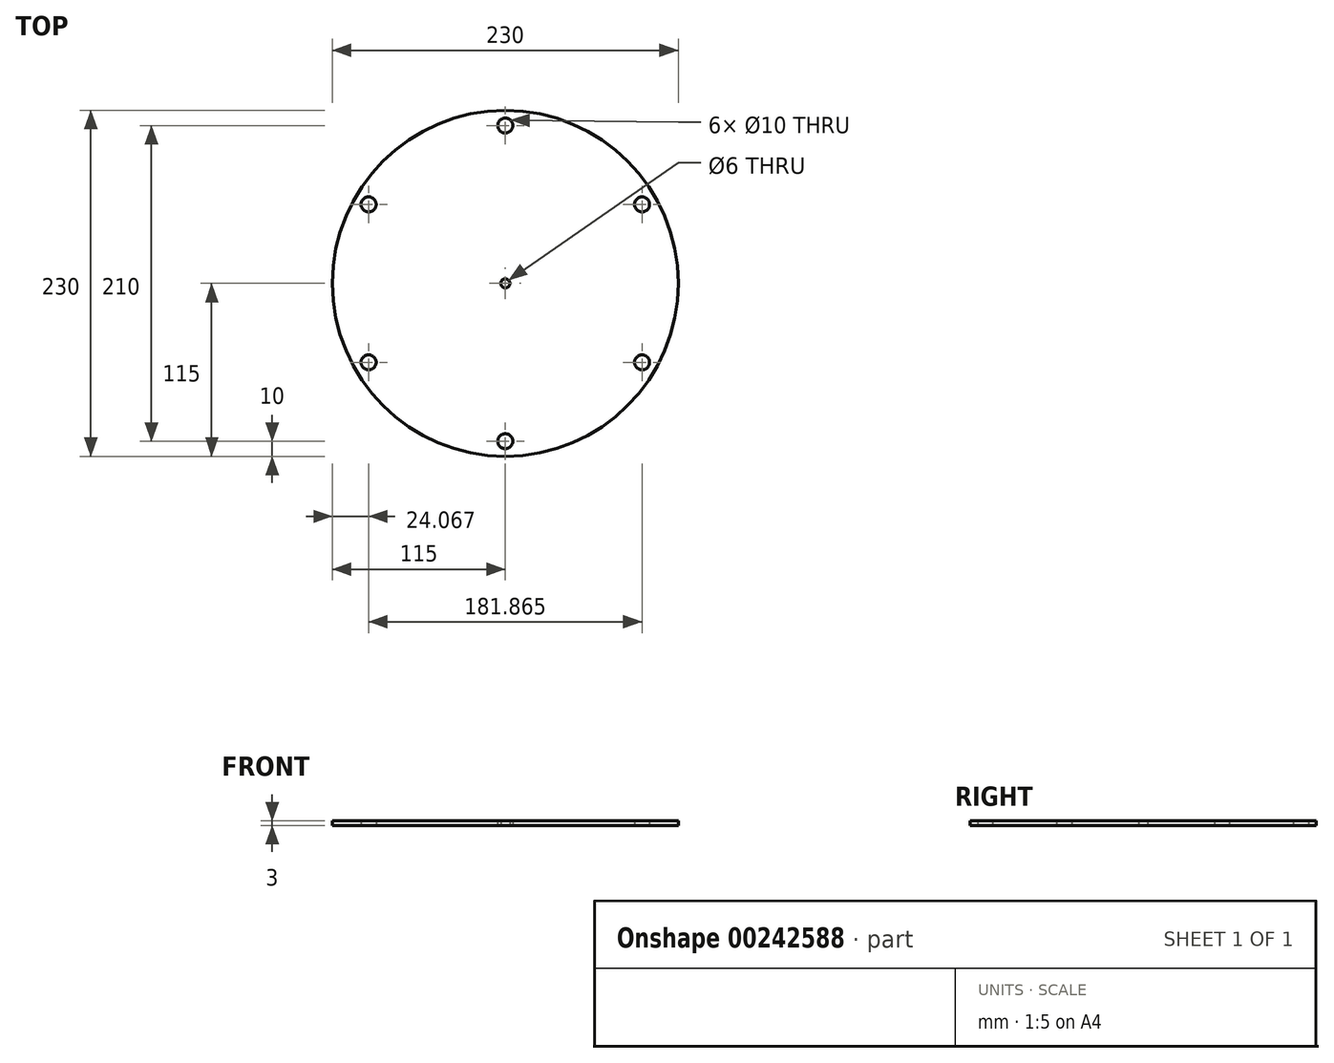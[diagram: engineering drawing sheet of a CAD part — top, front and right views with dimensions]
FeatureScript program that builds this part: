
annotation { "Feature Type Name" : "Feature", "Feature Type Description" : "" }
export const myFeature = defineFeature(function(context is Context, id is Id, definition is map)
    precondition{}
    {
        {
            var Q0;
            Q0=qCreatedBy(makeId("Top.planeOp"),FACE);
            var sketch = newSketch(context, id + "F0", { "sketchPlane" : qUnion([Q0])});
            skCircle(sketch, "E0", {"center": v(0, 0) * mm, "radius": 115 * mm});
            skCircle(sketch, "E1", {"center": v(0, 0) * mm, "radius": 3 * mm});
            skCircle(sketch, "E2", {"center": v(0, 105) * mm, "radius": 5 * mm});
            skCircle(sketch, "E3.1.0", {"center": v(-90.93, -52.5) * mm, "radius": 5 * mm});
            skCircle(sketch, "E3.2.0", {"center": v(90.93, -52.5) * mm, "radius": 5 * mm});
            skCircle(sketch, "E4.1.0", {"center": v(0, -105) * mm, "radius": 5 * mm});
            skCircle(sketch, "E4.1.1", {"center": v(90.93, 52.5) * mm, "radius": 5 * mm});
            skCircle(sketch, "E4.1.2", {"center": v(-90.93, 52.5) * mm, "radius": 5 * mm});
            skLineSegment(sketch, "E4.anchor1", {"start": v(0, 0) * mm, "end": v(-90.93, -52.5) * mm, "construction": true});
            skLineSegment(sketch, "E4.anchor2", {"start": v(0, 0) * mm, "end": v(90.93, 52.5) * mm, "construction": true});
            skSolve(sketch);
        }
        {
            var Q0;
            Q0 = qSketchRegion(id + "F0", true);
            extrude(context, id + "F1", {"entities" : qUnion([Q0]), "depth" : 3 * mm});
        }
    });
